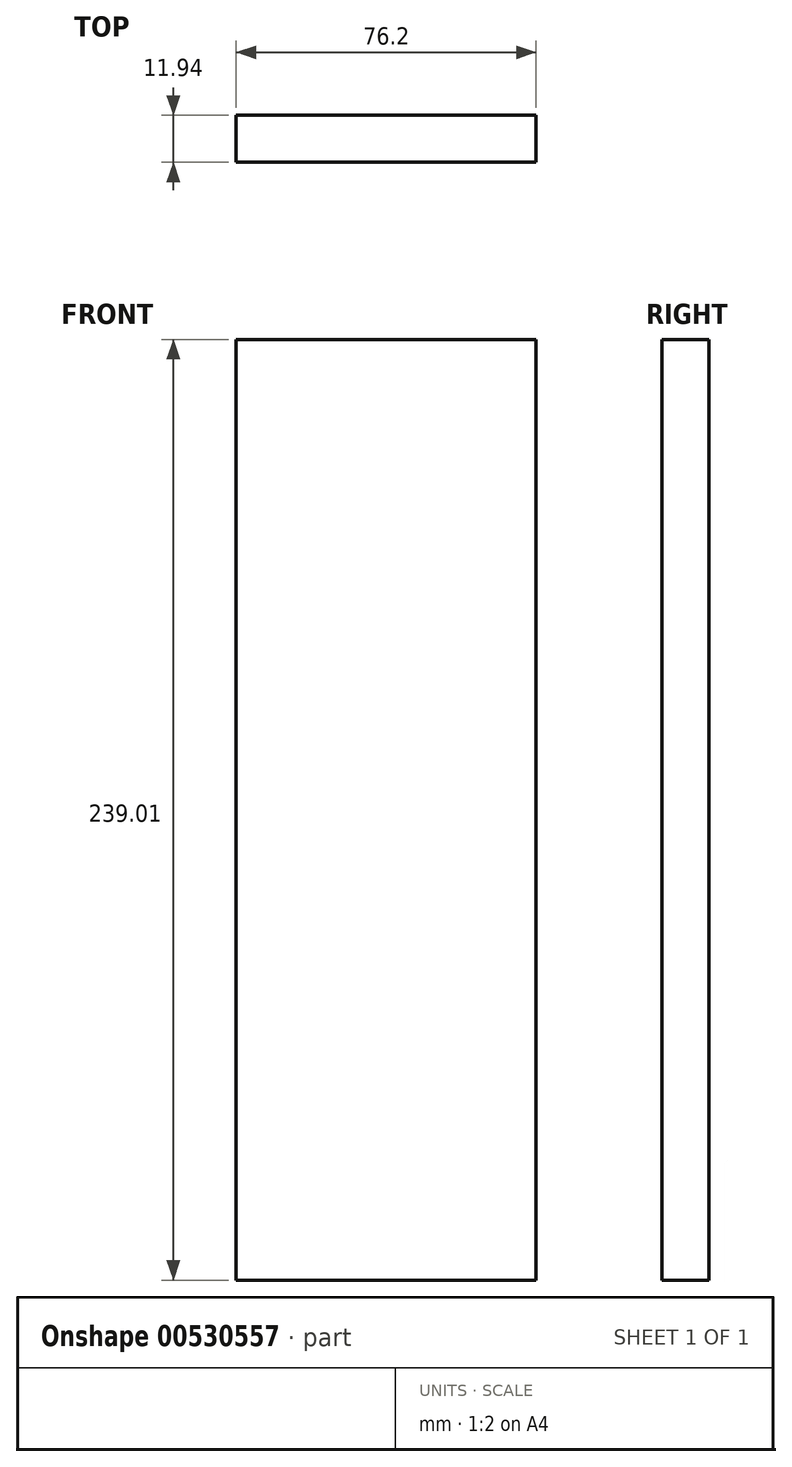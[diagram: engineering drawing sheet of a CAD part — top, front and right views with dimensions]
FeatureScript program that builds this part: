
annotation { "Feature Type Name" : "Feature", "Feature Type Description" : "" }
export const myFeature = defineFeature(function(context is Context, id is Id, definition is map)
    precondition{}
    {
        {
            var Q0;
            Q0=qCreatedBy(makeId("Front.planeOp"),FACE);
            var sketch = newSketch(context, id + "F0", { "sketchPlane" : qUnion([Q0])});
            skLineSegment(sketch, "E0.bottom", {"start": v(0, 0) * mm, "end": v(76.2, 0) * mm});
            skLineSegment(sketch, "E0.top", {"start": v(0, -239.01) * mm, "end": v(76.2, -239.01) * mm});
            skLineSegment(sketch, "E0.left", {"start": v(0, 0) * mm, "end": v(0, -239.01) * mm});
            skLineSegment(sketch, "E0.right", {"start": v(76.2, 0) * mm, "end": v(76.2, -239.01) * mm});
            skSolve(sketch);
        }
        {
            var Q0;
            Q0 = qSketchRegion(id + "F0", true);
            extrude(context, id + "F1", {"entities" : qUnion([Q0]), "depth" : 11.94 * mm, "offsetDistance" : 25.4 * mm});
        }
    });
